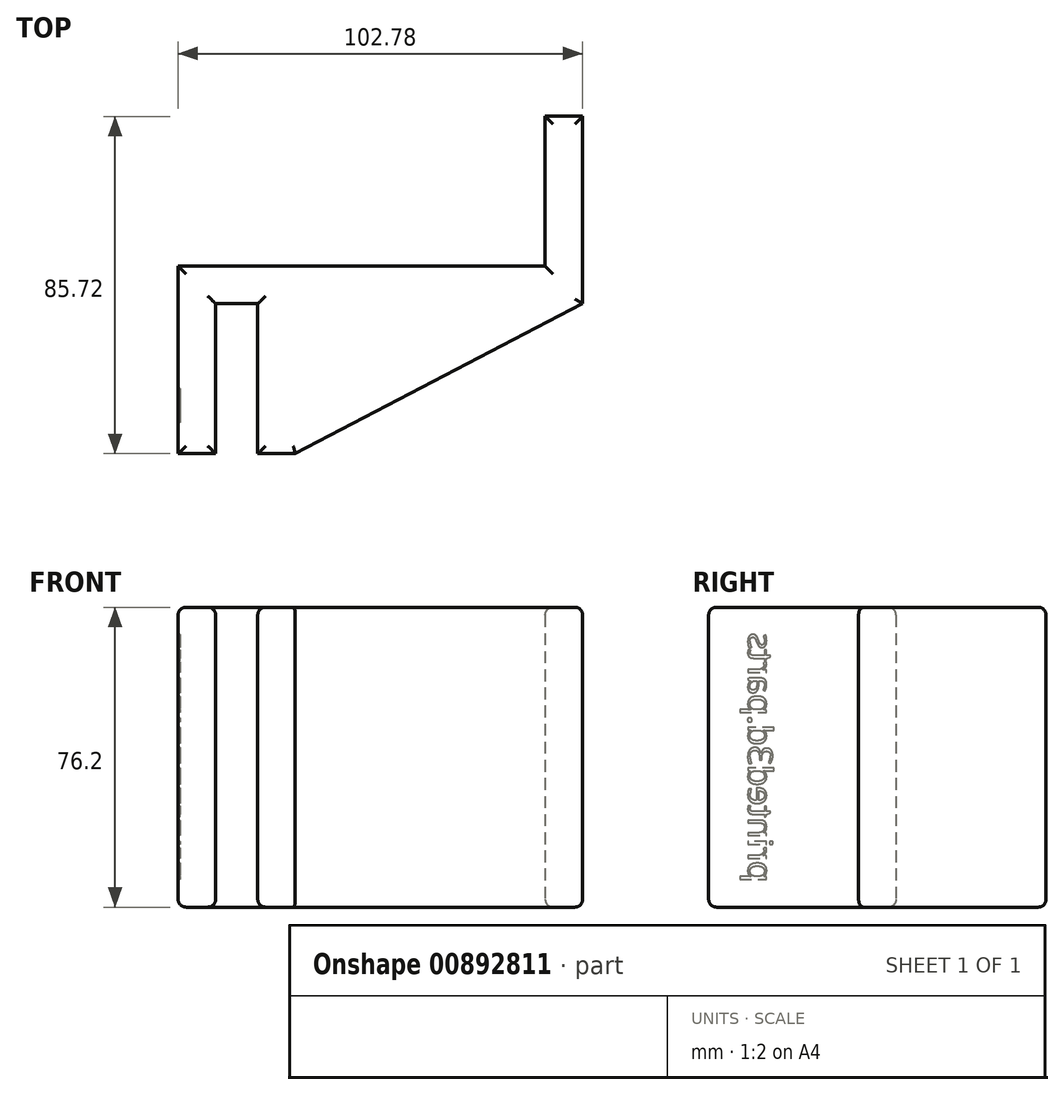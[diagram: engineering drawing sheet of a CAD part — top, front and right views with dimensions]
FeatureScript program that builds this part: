
annotation { "Feature Type Name" : "Feature", "Feature Type Description" : "" }
export const myFeature = defineFeature(function(context is Context, id is Id, definition is map)
    precondition{}
    {
        {
            var Q0;
            Q0=qCreatedBy(makeId("Top.planeOp"),FACE);
            var sketch = newSketch(context, id + "F0", { "sketchPlane" : qUnion([Q0])});
            skLineSegment(sketch, "E0", {"start": v(-29.75, -38.1) * mm, "end": v(-29.75, 9.52) * mm});
            skLineSegment(sketch, "E1", {"start": v(-29.75, 9.52) * mm, "end": v(63.5, 9.53) * mm});
            skLineSegment(sketch, "E2", {"start": v(63.5, 9.53) * mm, "end": v(63.5, 47.63) * mm});
            skLineSegment(sketch, "E3", {"start": v(63.5, 47.63) * mm, "end": v(73.03, 47.63) * mm});
            skLineSegment(sketch, "E4", {"start": v(73.03, 47.63) * mm, "end": v(73.03, 0) * mm});
            skLineSegment(sketch, "E5", {"start": v(73.03, 0) * mm, "end": v(0, 0) * mm});
            skLineSegment(sketch, "E6", {"start": v(0, 0) * mm, "end": v(0, -38.1) * mm});
            skLineSegment(sketch, "E7", {"start": v(0, -38.1) * mm, "end": v(-9.53, -38.1) * mm});
            skLineSegment(sketch, "E8", {"start": v(-9.53, -38.1) * mm, "end": v(-9.53, 0) * mm});
            skLineSegment(sketch, "E9", {"start": v(-9.53, 0) * mm, "end": v(-20.23, 0) * mm});
            skLineSegment(sketch, "E10", {"start": v(-20.23, 0) * mm, "end": v(-20.22, -38.1) * mm});
            skLineSegment(sketch, "E11", {"start": v(-20.22, -38.1) * mm, "end": v(-29.75, -38.1) * mm});
            skLineSegment(sketch, "E12", {"start": v(73.03, 0) * mm, "end": v(0, -38.1) * mm});
            skSolve(sketch);
        }
        {
            var Q0;
            Q0 = qSketchRegion(id + "F0", true);
            extrude(context, id + "F1", {"entities" : qUnion([Q0]), "depth" : 76.2 * mm, "offsetDistance" : 25 * mm});
        }
        {
            var Q0;
            Q0=makeQuery(id+"F1.opExtrude","CAP_FACE",FACE,{"disambiguationData":[OSD([sQuery(id+"F0.wireOp",EDGE,"E0"),sQuery(id+"F0.wireOp",EDGE,"E1"),sQuery(id+"F0.wireOp",EDGE,"E2"),sQuery(id+"F0.wireOp",EDGE,"E3"),sQuery(id+"F0.wireOp",EDGE,"E4"),sQuery(id+"F0.wireOp",EDGE,"E7"),sQuery(id+"F0.wireOp",EDGE,"E8"),sQuery(id+"F0.wireOp",EDGE,"E9"),sQuery(id+"F0.wireOp",EDGE,"E10"),sQuery(id+"F0.wireOp",EDGE,"E11"),sQuery(id+"F0.wireOp",EDGE,"E12")])],"isStart":true});
            var Q1;
            Q1=makeQuery(id+"F1.opExtrude","CAP_FACE",FACE,{"disambiguationData":[OSD([sQuery(id+"F0.wireOp",EDGE,"E0"),sQuery(id+"F0.wireOp",EDGE,"E1"),sQuery(id+"F0.wireOp",EDGE,"E2"),sQuery(id+"F0.wireOp",EDGE,"E3"),sQuery(id+"F0.wireOp",EDGE,"E4"),sQuery(id+"F0.wireOp",EDGE,"E7"),sQuery(id+"F0.wireOp",EDGE,"E8"),sQuery(id+"F0.wireOp",EDGE,"E9"),sQuery(id+"F0.wireOp",EDGE,"E10"),sQuery(id+"F0.wireOp",EDGE,"E11"),sQuery(id+"F0.wireOp",EDGE,"E12")])],"isStart":false});
            fillet(context, id + "F2", {"entities" : qUnion([Q0, Q1]), "radius" : 2 * mm, "tangentPropagation" : true, "allowEdgeOverflow" : false});
        }
        {
            var Q0;
            Q0=makeQuery(id+"F1.opExtrude","SWEPT_FACE",FACE,{"disambiguationData":[OSD([sQuery(id+"F0.wireOp",EDGE,"E0")])]});
            var sketch = newSketch(context, id + "F3", { "sketchPlane" : qUnion([Q0])});
            skText(sketch, "E13", { "text": "printed3d.parts", "fontName": "OpenSans-Regular.ttf"});
            skLineSegment(sketch, "E14", {"start": v(38.1, 38.1) * mm, "end": v(-9.52, 38.1) * mm, "construction": true});
            const initialGuessF3  = {"E13": [0.0281, 0.00635, 0, 1, 0.00627]};
            skSetInitialGuess(sketch, initialGuessF3);
            skSolve(sketch);
        }
        {
            var Q0;
            Q0 = qSketchRegion(id + "F3", true);
            extrude(context, id + "F4", {"entities" : qUnion([Q0]), "operationType" : NewBodyOperationType.REMOVE, "oppositeDirection" : true, "depth" : 0.5 * mm, "offsetDistance" : 25 * mm});
        }
    });
